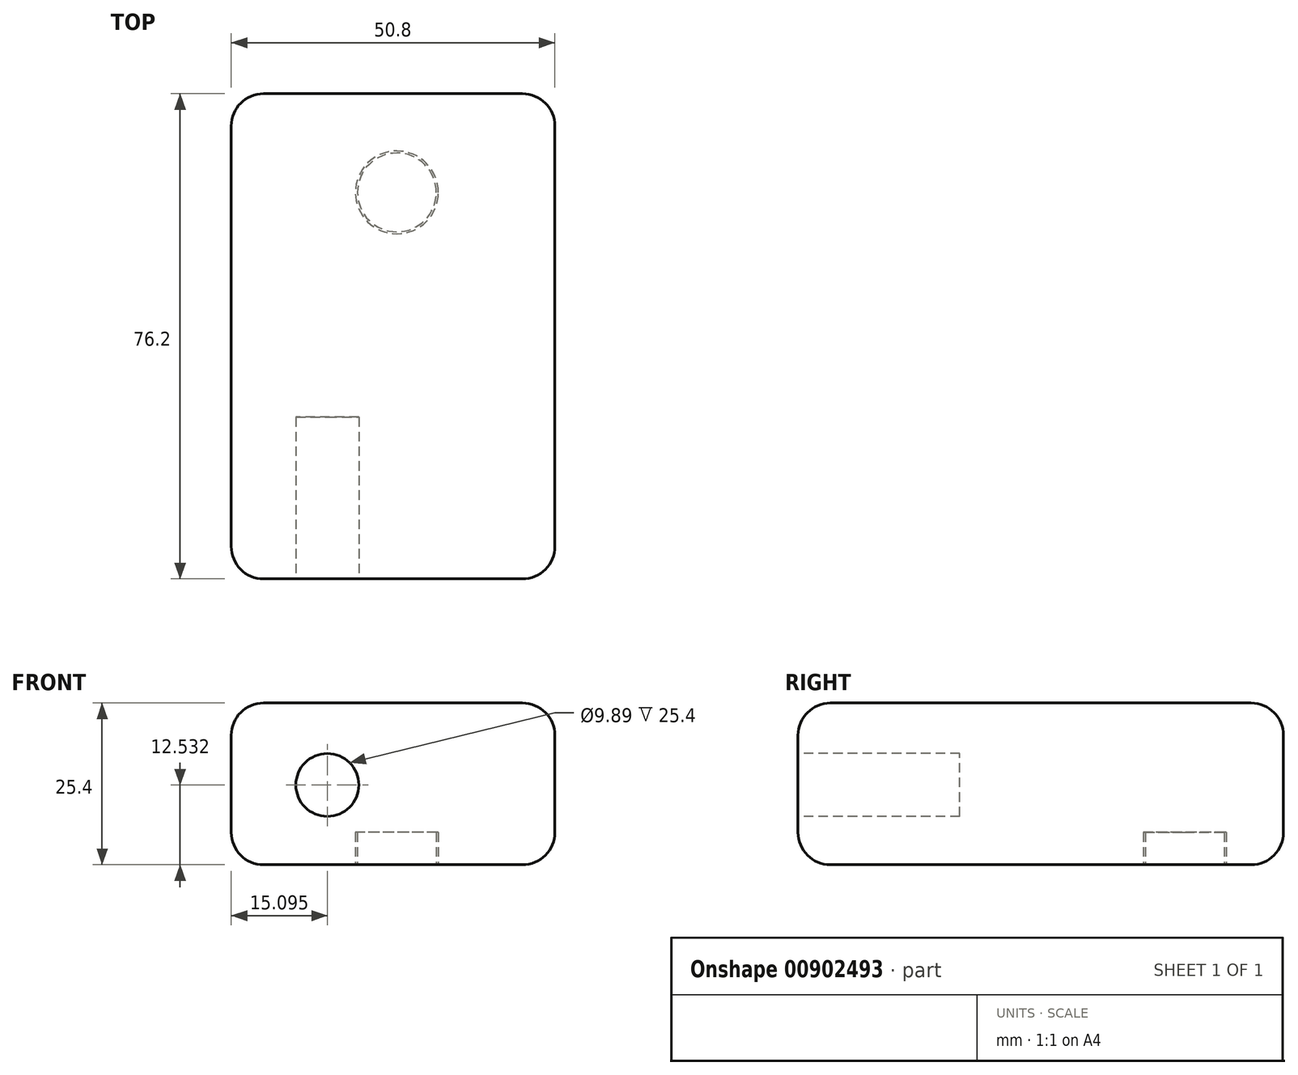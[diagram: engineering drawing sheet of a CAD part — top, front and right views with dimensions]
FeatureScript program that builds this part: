
annotation { "Feature Type Name" : "Feature", "Feature Type Description" : "" }
export const myFeature = defineFeature(function(context is Context, id is Id, definition is map)
    precondition{}
    {
        {
            var Q0;
            Q0=qCreatedBy(makeId("Top.planeOp"),FACE);
            var sketch = newSketch(context, id + "F0", { "sketchPlane" : qUnion([Q0])});
            skLineSegment(sketch, "E0.bottom", {"start": v(0, 0) * mm, "end": v(50.8, 0) * mm});
            skLineSegment(sketch, "E0.top", {"start": v(0, -76.2) * mm, "end": v(50.8, -76.2) * mm});
            skLineSegment(sketch, "E0.left", {"start": v(0, 0) * mm, "end": v(0, -76.2) * mm});
            skLineSegment(sketch, "E0.right", {"start": v(50.8, 0) * mm, "end": v(50.8, -76.2) * mm});
            skSolve(sketch);
        }
        {
            var Q0;
            Q0 = qSketchRegion(id + "F0", true);
            extrude(context, id + "F1", {"entities" : qUnion([Q0]), "depth" : 25.4 * mm, "offsetDistance" : 25.4 * mm});
        }
        {
            var Q0;
            Q0=makeQuery(id+"F1.opExtrude","SWEPT_EDGE",EDGE,{"disambiguationData":[OSD([sQuery(id+"F0.wireOp",EDGE,"E0.top"),sQuery(id+"F0.wireOp",EDGE,"E0.left")])]});
            var Q1;
            Q1=makeQuery(id+"F1.opExtrude","SWEPT_EDGE",EDGE,{"disambiguationData":[OSD([sQuery(id+"F0.wireOp",EDGE,"E0.top"),sQuery(id+"F0.wireOp",EDGE,"E0.right")])]});
            var Q2;
            Q2=makeQuery(id+"F1.opExtrude","SWEPT_EDGE",EDGE,{"disambiguationData":[OSD([sQuery(id+"F0.wireOp",EDGE,"E0.bottom"),sQuery(id+"F0.wireOp",EDGE,"E0.right")])]});
            var Q3;
            Q3=makeQuery(id+"F1.opExtrude","SWEPT_EDGE",EDGE,{"disambiguationData":[OSD([sQuery(id+"F0.wireOp",EDGE,"E0.bottom"),sQuery(id+"F0.wireOp",EDGE,"E0.left")])]});
            fillet(context, id + "F2", {"entities" : qUnion([Q0, Q1, Q2, Q3]), "radius" : 5.08 * mm, "tangentPropagation" : true, "allowEdgeOverflow" : false});
        }
        {
            var Q0;
            Q0=makeQuery(id+"F1.opExtrude","SWEPT_FACE",FACE,{"disambiguationData":[OSD([sQuery(id+"F0.wireOp",EDGE,"E0.top")])]});
            var sketch = newSketch(context, id + "F3", { "sketchPlane" : qUnion([Q0])});
            skCircle(sketch, "E1", {"center": v(15.1, 12.53) * mm, "radius": 4.94 * mm});
            skSolve(sketch);
        }
        {
            var Q0;
            Q0 = qSketchRegion(id + "F3", true);
            extrude(context, id + "F4", {"entities" : qUnion([Q0]), "operationType" : NewBodyOperationType.REMOVE, "oppositeDirection" : true, "depth" : 25.4 * mm, "offsetDistance" : 25.4 * mm});
        }
        {
            var Q0;
            Q0=makeQuery(id+"F1.opExtrude","CAP_EDGE",EDGE,{"disambiguationData":[OSD([sQuery(id+"F0.wireOp",EDGE,"E0.top")])],"isStart":false});
            var Q1;
            Q1=makeQuery(id+"F1.opExtrude","CAP_EDGE",EDGE,{"disambiguationData":[OSD([sQuery(id+"F0.wireOp",EDGE,"E0.top")])],"isStart":true});
            fillet(context, id + "F5", {"entities" : qUnion([Q0, Q1]), "radius" : 5.08 * mm, "tangentPropagation" : true, "allowEdgeOverflow" : false});
        }
        {
            var Q0;
            Q0=makeQuery(id+"F0.imprint","IMPRINT",FACE,{"disambiguationData":[TD([[makeQuery(id+"F0.imprint","IMPRINT",EDGE,{"derivedFrom":sQuery(id+"F0.wireOp",EDGE,"E0.bottom")}),-1.0]])]});
            var sketch = newSketch(context, id + "F6", { "sketchPlane" : qUnion([Q0])});
            skCircle(sketch, "E2", {"center": v(26, -15.5) * mm, "radius": 6.5 * mm});
            skCircle(sketch, "E3", {"center": v(26, -15.5) * mm, "radius": 6.2 * mm});
            skSolve(sketch);
        }
        {
            var Q0;
            Q0 = qSketchRegion(id + "F6", true);
            extrude(context, id + "F7", {"entities" : qUnion([Q0]), "operationType" : NewBodyOperationType.REMOVE, "depth" : 5.08 * mm, "offsetDistance" : 25.4 * mm});
        }
    });
